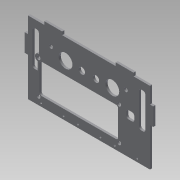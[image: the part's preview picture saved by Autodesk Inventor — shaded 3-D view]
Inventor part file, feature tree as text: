
AUTODESK INVENTOR PART (.ipt)
format: ipt  version: 2015 SP1 (Build 190203100, 203)  size: 916,992 bytes
history: native  units: mm
features: extrude x5, sketch x3, fillet x1
ambient origin geometry x8: Origin, YZ Plane, XZ Plane, XY Plane, X Axis, Y Axis, Z Axis, Center Point
bodies: Solid1 (feature_tree)
feature tree (9):
  sketch  "Sketch1"  dims[d20=6.0mm d21=0.0mm]
  extrude  "Extrusion1"  TaperAngle=0.0deg  [1 undecoded]
  sketch  "Sketch2"  dims[d22=7.353mm d23=1.598861mm]
  extrude  "Extrusion3"  Depth=1.598861mm
  extrude  "Extrusion4"  Depth=2.0mm
  extrude  "Extrusion5"  Depth=2.0mm
  extrude  "Extrusion6"  Depth=2.0mm
  fillet  "Fillet2"  Radius=6.0mm
  sketch  "Sketch3"  dims[d27=43.688mm d28=21.844mm d30=3.1mm d32=11.75mm d33=6.0mm d34=6.604mm d35=6.604mm d38=13.691mm d41=2.0mm d42=0.0mm d45=70.0mm d46=1.598861mm d47=1.598861mm d48=2.0mm d49=0.0mm d52=7.5mm d53=2.0mm d59=2.0mm d60=0.0mm d61=26.0mm d62=71.7mm d63=31.2mm d64=75.25mm d67=2.6mm d70=1.775mm d71=10.4mm d72=1.0mm d73=0.0mm d74=0.891933mm d75=1.0mm d76=0.0mm d77=2.0mm]
note: 1 required parameter value undecoded (feature->parameter linkage not recoverable at this tier; creation-order binding heuristic only, values carry confidence <= 0.55)
